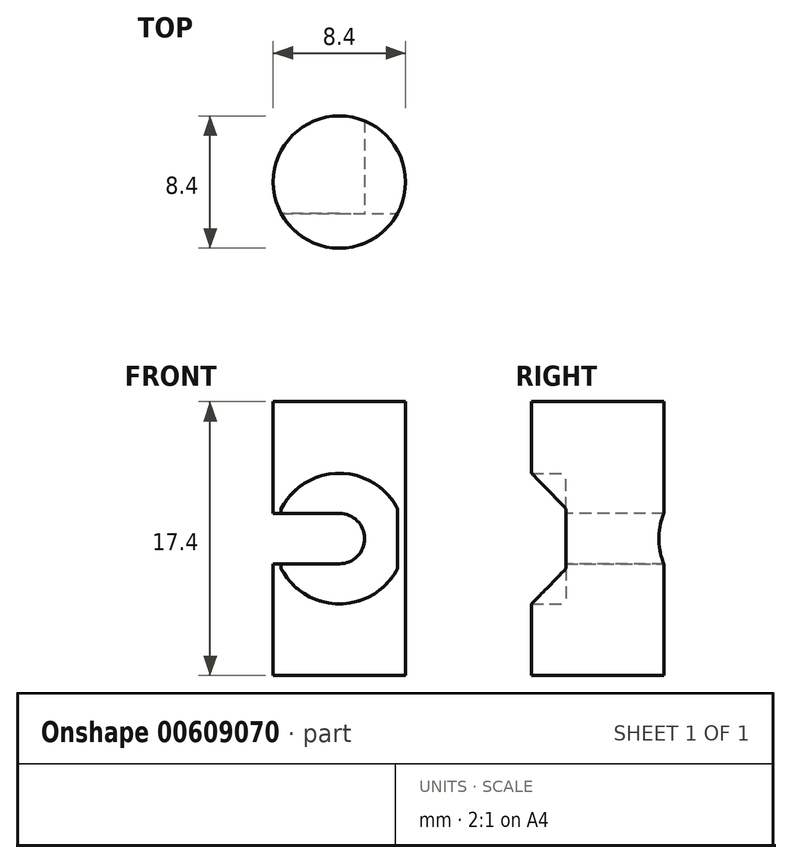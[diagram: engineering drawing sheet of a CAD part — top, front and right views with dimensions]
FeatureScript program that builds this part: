
annotation { "Feature Type Name" : "Feature", "Feature Type Description" : "" }
export const myFeature = defineFeature(function(context is Context, id is Id, definition is map)
    precondition{}
    {
        {
            var Q0;
            Q0=qCreatedBy(makeId("Top.planeOp"),FACE);
            var sketch = newSketch(context, id + "F0", { "sketchPlane" : qUnion([Q0])});
            skCircle(sketch, "E0", {"center": v(0, 0) * mm, "radius": 4.2 * mm});
            skSolve(sketch);
        }
        {
            var Q0;
            Q0=qCreatedBy(makeId("Front.planeOp"),FACE);
            var sketch = newSketch(context, id + "F1", { "sketchPlane" : qUnion([Q0])});
            skCircle(sketch, "E1", {"center": v(0, 0) * mm, "radius": 4.15 * mm});
            skCircle(sketch, "E2", {"center": v(0, 0) * mm, "radius": 1.6 * mm});
            skLineSegment(sketch, "E3", {"start": v(0, 1.6) * mm, "end": v(-4.2, 1.6) * mm});
            skLineSegment(sketch, "E4", {"start": v(-4.2, 1.6) * mm, "end": v(-4.2, -1.6) * mm});
            skLineSegment(sketch, "E5", {"start": v(-4.2, -1.6) * mm, "end": v(0, -1.6) * mm});
            skLineSegment(sketch, "E6", {"start": v(-4.15, 4.15) * mm, "end": v(4.15, 4.15) * mm});
            skLineSegment(sketch, "E7", {"start": v(4.15, 4.15) * mm, "end": v(4.15, -4.15) * mm});
            skLineSegment(sketch, "E8", {"start": v(4.15, -4.15) * mm, "end": v(-4.15, -4.15) * mm});
            skLineSegment(sketch, "E9", {"start": v(-4.15, -4.15) * mm, "end": v(-4.15, 4.15) * mm});
            skSolve(sketch);
        }
        {
            var Q0;
            Q0=makeQuery(id+"F0.imprint","IMPRINT",FACE,{"disambiguationData":[TD([[makeQuery(id+"F0.imprint","IMPRINT",EDGE,{"derivedFrom":sQuery(id+"F0.wireOp",EDGE,"E0")}),1.0]])]});
            var Q1;
            Q1 = qSketchRegion(id + "F0", true);
            extrude(context, id + "F2", {"entities" : qUnion([Q0, Q1]), "depth" : (17.4 / 2) * mm, "offsetDistance" : 25 * mm, "hasSecondDirection" : true, "secondDirectionOppositeDirection" : true, "secondDirectionDepth" : 8.7 * mm});
        }
        {
            var Q0;
            {var subQ0=sQuery(id+"F1.wireOp",EDGE,"E1");var subQ4=makeQuery(id+"F1.imprint","INTERSECT",VERTEX,{"derivedFrom":[subQ0,sQuery(id+"F1.wireOp",EDGE,"E6")]});Q0=makeQuery(id+"F1.imprint","IMPRINT",FACE,{"disambiguationData":[TD([[makeQuery(id+"F1.imprint","IMPRINT",EDGE,{"disambiguationData":[TD([[subQ4,1.0]])],"derivedFrom":subQ0}),1.0]])]});}
            extrude(context, id + "F3", {"entities" : qUnion([Q0]), "operationType" : NewBodyOperationType.REMOVE, "depth" : 5 * mm, "offsetDistance" : 25 * mm, "hasSecondDirection" : true, "secondDirectionOppositeDirection" : false, "secondDirectionDepth" : 2 * mm});
        }
        {
            var Q0;
            {var subQ0=sQuery(id+"F1.wireOp",EDGE,"E3");var subQ5=sQuery(id+"F1.wireOp",EDGE,"E1");var subQ6=makeQuery(id+"F1.imprint","INTERSECT",VERTEX,{"derivedFrom":[subQ5,subQ0]});Q0=makeQuery(id+"F1.imprint","IMPRINT",FACE,{"disambiguationData":[TD([[makeQuery(id+"F1.imprint","IMPRINT",EDGE,{"disambiguationData":[TD([[subQ6,-1.0]])],"derivedFrom":subQ5}),1.0]])]});}
            var Q1;
            {var subQ0=sQuery(id+"F1.wireOp",EDGE,"E2");var subQ1=makeQuery(id+"F1.imprint","INTERSECT",VERTEX,{"derivedFrom":[subQ0,sQuery(id+"F1.wireOp",EDGE,"E3")]});Q1=makeQuery(id+"F1.imprint","IMPRINT",FACE,{"disambiguationData":[TD([[makeQuery(id+"F1.imprint","IMPRINT",EDGE,{"disambiguationData":[TD([[subQ1,-1.0]])],"derivedFrom":subQ0}),1.0]])]});}
            var Q2;
            {var subQ0=sQuery(id+"F1.wireOp",EDGE,"E9");var subQ1=sQuery(id+"F1.wireOp",EDGE,"E1");var subQ2=makeQuery(id+"F1.imprint","INTERSECT",VERTEX,{"derivedFrom":[subQ1,subQ0]});Q2=makeQuery(id+"F1.imprint","IMPRINT",FACE,{"disambiguationData":[TD([[makeQuery(id+"F1.imprint","IMPRINT",EDGE,{"disambiguationData":[TD([[subQ2,-1.0]])],"derivedFrom":subQ1}),-1.0]])]});}
            var Q3;
            {var subQ0=sQuery(id+"F1.wireOp",EDGE,"E3");var subQ1=sQuery(id+"F1.wireOp",EDGE,"E1");var subQ2=makeQuery(id+"F1.imprint","INTERSECT",VERTEX,{"derivedFrom":[subQ1,subQ0]});Q3=makeQuery(id+"F1.imprint","IMPRINT",FACE,{"disambiguationData":[TD([[makeQuery(id+"F1.imprint","IMPRINT",EDGE,{"disambiguationData":[TD([[subQ2,-1.0]])],"derivedFrom":subQ1}),-1.0]])]});}
            var Q4;
            {var subQ4=sQuery(id+"F1.wireOp",EDGE,"E4");Q4=makeQuery(id+"F1.imprint","IMPRINT",FACE,{"disambiguationData":[TD([[makeQuery(id+"F1.imprint","IMPRINT",EDGE,{"derivedFrom":subQ4}),1.0]])]});}
            extrude(context, id + "F4", {"entities" : qUnion([Q0, Q1, Q2, Q3, Q4]), "operationType" : NewBodyOperationType.REMOVE, "oppositeDirection" : true, "depth" : 25 * mm, "offsetDistance" : 25 * mm, "hasSecondDirection" : true, "secondDirectionOppositeDirection" : false, "secondDirectionDepth" : 25 * mm});
        }
    });
